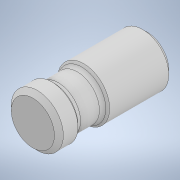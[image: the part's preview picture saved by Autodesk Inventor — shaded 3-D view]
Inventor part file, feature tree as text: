
AUTODESK INVENTOR PART (.ipt)
format: ipt  version: 2020 (Build 240168000, 168)  size: 138,752 bytes
history: native  units: mm
features: extrude x3, sketch x3, chamfer x2, other x1, fillet x1
ambient origin geometry x8: Origin, YZ Plane, XZ Plane, XY Plane, X Axis, Y Axis, Z Axis, Center Point
bodies: Body1 (feature_tree)
feature tree (10):
  other  "ソリッド1"
  extrude  "押し出し1"  Depth=8.2mm
  extrude  "押し出し2"  Depth=10.0mm TaperAngle=0.0deg
  extrude  "押し出し3"  Depth=7.0mm
  chamfer  "面取り1"  Distance=5.0mm
  chamfer  "面取り2"  Distance=3.0mm
  fillet  "フィレット1"  Radius=0.6mm
  sketch  "スケッチ1"
  sketch  "スケッチ2"
  sketch  "スケッチ3"
